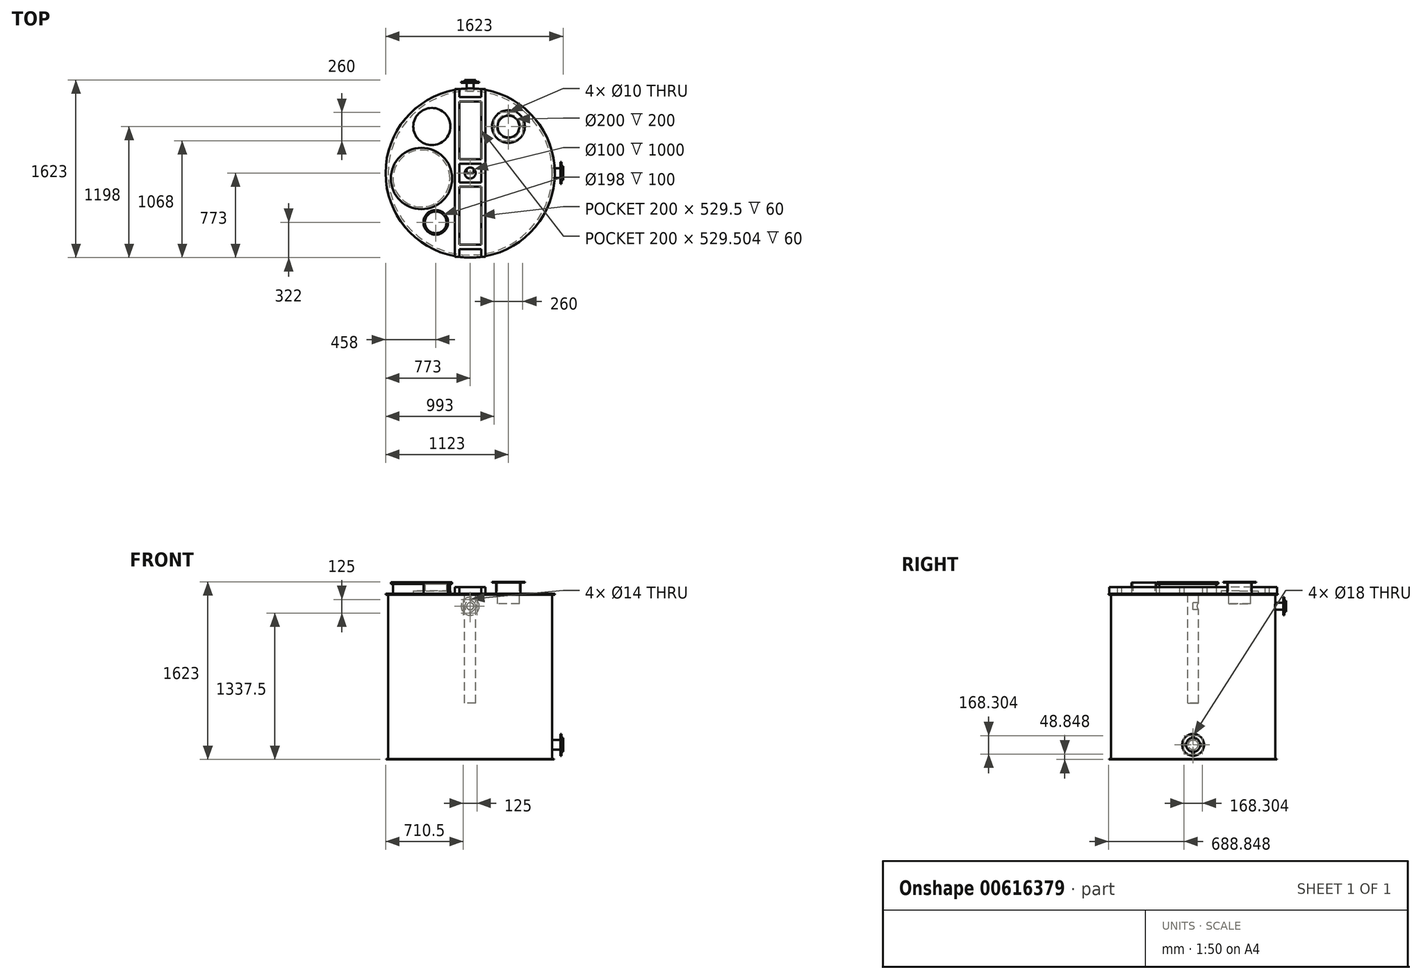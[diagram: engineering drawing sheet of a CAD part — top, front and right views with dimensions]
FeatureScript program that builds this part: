
annotation { "Feature Type Name" : "Feature", "Feature Type Description" : "" }
export const myFeature = defineFeature(function(context is Context, id is Id, definition is map)
    precondition{}
    {
        {
            var Q0;
            Q0=qCreatedBy(makeId("Front.planeOp"),FACE);
            var sketch = newSketch(context, id + "F0", { "sketchPlane" : qUnion([Q0])});
            skLineSegment(sketch, "E0.bottom", {"start": v(0, 0) * mm, "end": v(750, 0) * mm});
            skLineSegment(sketch, "E0.top", {"start": v(0, 1515) * mm, "end": v(750, 1515) * mm});
            skLineSegment(sketch, "E0.left", {"start": v(0, 0) * mm, "end": v(0, 1515) * mm});
            skLineSegment(sketch, "E0.right", {"start": v(750, 5) * mm, "end": v(750, 1505) * mm});
            skLineSegment(sketch, "E1.bottom", {"start": v(750, 0) * mm, "end": v(768.5, 0) * mm});
            skLineSegment(sketch, "E1.top", {"start": v(750, 5) * mm, "end": v(768.5, 5) * mm});
            skLineSegment(sketch, "E1.right", {"start": v(768.5, 0) * mm, "end": v(768.5, 5) * mm});
            skLineSegment(sketch, "E2.bottom", {"start": v(750, 1515) * mm, "end": v(773, 1515) * mm});
            skLineSegment(sketch, "E2.top", {"start": v(750, 1505) * mm, "end": v(773, 1505) * mm});
            skLineSegment(sketch, "E2.right", {"start": v(773, 1515) * mm, "end": v(773, 1505) * mm});
            skSolve(sketch);
        }
        {
            var Q0;
            Q0=makeQuery(id+"F0.imprint","IMPRINT",FACE,{"disambiguationData":[TD([[makeQuery(id+"F0.imprint","IMPRINT",EDGE,{"derivedFrom":sQuery(id+"F0.wireOp",EDGE,"E0.bottom")}),1.0]])]});
            var Q1;
            Q1=sQuery(id+"F0.wireOp",EDGE,"E0.left");
            revolve(context, id + "F1", {"entities" : qUnion([Q0]), "axis" : qUnion([Q1]), "revolveType" : RevolveType.FULL});
        }
        {
            var Q0;
            Q0=makeQuery(id+"F1.opRevolve","SWEPT_FACE",FACE,{"disambiguationData":[OSD([sQuery(id+"F0.wireOp",EDGE,"E0.top"),sQuery(id+"F0.wireOp",EDGE,"E2.bottom")])]});
            var sketch = newSketch(context, id + "F2", { "sketchPlane" : qUnion([Q0])});
            skLineSegment(sketch, "E3.bottom", {"start": v(-140, 766.5) * mm, "end": v(-100, 766.5) * mm});
            skLineSegment(sketch, "E3.top", {"start": v(-140, -766.5) * mm, "end": v(-100, -766.5) * mm});
            skLineSegment(sketch, "E3.left", {"start": v(-140, 766.5) * mm, "end": v(-140, -766.5) * mm});
            skLineSegment(sketch, "E3.right", {"start": v(-100, 766.5) * mm, "end": v(-100, 694.5) * mm});
            skLineSegment(sketch, "E4.bottom", {"start": v(100, 766.5) * mm, "end": v(140, 766.5) * mm});
            skLineSegment(sketch, "E4.top", {"start": v(100, -766.5) * mm, "end": v(140, -766.5) * mm});
            skLineSegment(sketch, "E4.left", {"start": v(100, 766.5) * mm, "end": v(100, 694.5) * mm});
            skLineSegment(sketch, "E4.right", {"start": v(140, 766.5) * mm, "end": v(140, -766.5) * mm});
            skLineSegment(sketch, "E5.bottom", {"start": v(-100, 694.5) * mm, "end": v(100, 694.5) * mm});
            skLineSegment(sketch, "E5.top", {"start": v(-100, 654.5) * mm, "end": v(100, 654.5) * mm});
            skLineSegment(sketch, "E6.bottom", {"start": v(-100, -654.5) * mm, "end": v(100, -654.5) * mm});
            skLineSegment(sketch, "E6.top", {"start": v(-100, -694.5) * mm, "end": v(100, -694.5) * mm});
            skLineSegment(sketch, "E7.bottom", {"start": v(-100, 125) * mm, "end": v(100, 125) * mm});
            skLineSegment(sketch, "E7.top", {"start": v(-100, 85) * mm, "end": v(100, 85) * mm});
            skLineSegment(sketch, "E8.bottom", {"start": v(-100, -85) * mm, "end": v(100, -85) * mm});
            skLineSegment(sketch, "E8.top", {"start": v(-100, -125) * mm, "end": v(100, -125) * mm});
            skLineSegment(sketch, "E9.trimOffspring", {"start": v(-100, 654.5) * mm, "end": v(-100, 125) * mm});
            skLineSegment(sketch, "E10.trimOffspring", {"start": v(100, 654.5) * mm, "end": v(100, 125) * mm});
            skLineSegment(sketch, "E11.trimOffspring", {"start": v(-100, 85) * mm, "end": v(-100, -85) * mm});
            skLineSegment(sketch, "E12.trimOffspring", {"start": v(100, 85) * mm, "end": v(100, -85) * mm});
            skLineSegment(sketch, "E13.trimOffspring", {"start": v(-100, -125) * mm, "end": v(-100, -654.5) * mm});
            skLineSegment(sketch, "E14.trimOffspring", {"start": v(100, -125) * mm, "end": v(100, -654.5) * mm});
            skLineSegment(sketch, "E15.trimOffspring", {"start": v(-100, -694.5) * mm, "end": v(-100, -766.5) * mm});
            skLineSegment(sketch, "E16.trimOffspring", {"start": v(100, -694.5) * mm, "end": v(100, -766.5) * mm});
            skSolve(sketch);
        }
        {
            var Q0;
            Q0 = qSketchRegion(id + "F2", true);
            extrude(context, id + "F3", {"entities" : qUnion([Q0]), "operationType" : NewBodyOperationType.ADD, "depth" : 60 * mm, "offsetDistance" : 25 * mm});
        }
        {
            var Q0;
            {var subQ0=sQuery(id+"F2.wireOp",EDGE,"E3.left");Q0=makeQuery(id+"F3.boolean.opBoolean","SPLIT",FACE,{"disambiguationData":[TD([makeQuery(id+"F3.opExtrude","SWEPT_FACE",FACE,{"disambiguationData":[OSD([subQ0])]})])],"derivedFrom":makeQuery(id+"F1.opRevolve","SWEPT_FACE",FACE,{"disambiguationData":[OSD([sQuery(id+"F0.wireOp",EDGE,"E0.top"),sQuery(id+"F0.wireOp",EDGE,"E2.bottom")])]})});}
            var sketch = newSketch(context, id + "F4", { "sketchPlane" : qUnion([Q0])});
            skCircle(sketch, "E17", {"center": v(-445, -50) * mm, "radius": 260 * mm});
            skSolve(sketch);
        }
        {
            var Q0;
            Q0=makeQuery(id+"F4.imprint","IMPRINT",FACE,{"disambiguationData":[TD([[makeQuery(id+"F4.imprint","IMPRINT",EDGE,{"derivedFrom":sQuery(id+"F4.wireOp",EDGE,"E17")}),1.0]])]});
            extrude(context, id + "F5", {"entities" : qUnion([Q0]), "operationType" : NewBodyOperationType.ADD, "depth" : 90 * mm, "offsetDistance" : 25 * mm});
        }
        {
            var Q0;
            {var subQ0=sQuery(id+"F2.wireOp",EDGE,"E3.left");Q0=makeQuery(id+"F3.boolean.opBoolean","SPLIT",FACE,{"disambiguationData":[TD([makeQuery(id+"F3.opExtrude","SWEPT_FACE",FACE,{"disambiguationData":[OSD([subQ0])]})])],"derivedFrom":makeQuery(id+"F1.opRevolve","SWEPT_FACE",FACE,{"disambiguationData":[OSD([sQuery(id+"F0.wireOp",EDGE,"E0.top"),sQuery(id+"F0.wireOp",EDGE,"E2.bottom")])]})});}
            var sketch = newSketch(context, id + "F6", { "sketchPlane" : qUnion([Q0])});
            skCircle(sketch, "E18", {"center": v(-350, 425) * mm, "radius": 170 * mm});
            skSolve(sketch);
        }
        {
            var Q0;
            Q0=makeQuery(id+"F6.imprint","IMPRINT",FACE,{"disambiguationData":[TD([[makeQuery(id+"F6.imprint","IMPRINT",EDGE,{"derivedFrom":sQuery(id+"F6.wireOp",EDGE,"E18")}),1.0]])]});
            extrude(context, id + "F7", {"entities" : qUnion([Q0]), "operationType" : NewBodyOperationType.ADD, "depth" : 25 * mm, "offsetDistance" : 25 * mm});
        }
        {
            var Q0;
            Q0=makeQuery(id+"F5.opExtrude","CAP_FACE",FACE,{"disambiguationData":[OSD([sQuery(id+"F4.wireOp",EDGE,"E17")])],"isStart":false});
            var sketch = newSketch(context, id + "F8", { "sketchPlane" : qUnion([Q0])});
            skCircle(sketch, "E19", {"center": v(-445, -50) * mm, "radius": 280 * mm});
            skSolve(sketch);
        }
        {
            var Q0;
            Q0 = qSketchRegion(id + "F8", true);
            extrude(context, id + "F9", {"entities" : qUnion([Q0]), "operationType" : NewBodyOperationType.ADD, "depth" : 15 * mm, "offsetDistance" : 25 * mm});
        }
        {
            var Q0;
            {var subQ0=sQuery(id+"F2.wireOp",EDGE,"E4.right");Q0=makeQuery(id+"F3.boolean.opBoolean","SPLIT",FACE,{"disambiguationData":[TD([makeQuery(id+"F3.opExtrude","SWEPT_FACE",FACE,{"disambiguationData":[OSD([subQ0])]})])],"derivedFrom":makeQuery(id+"F1.opRevolve","SWEPT_FACE",FACE,{"disambiguationData":[OSD([sQuery(id+"F0.wireOp",EDGE,"E0.top"),sQuery(id+"F0.wireOp",EDGE,"E2.bottom")])]})});}
            var sketch = newSketch(context, id + "F10", { "sketchPlane" : qUnion([Q0])});
            skCircle(sketch, "E20", {"center": v(350, 425) * mm, "radius": 111 * mm});
            skSolve(sketch);
        }
        {
            var Q0;
            Q0=makeQuery(id+"F10.imprint","IMPRINT",FACE,{"disambiguationData":[TD([[makeQuery(id+"F10.imprint","IMPRINT",EDGE,{"derivedFrom":sQuery(id+"F10.wireOp",EDGE,"E20")}),1.0]])]});
            extrude(context, id + "F11", {"entities" : qUnion([Q0]), "operationType" : NewBodyOperationType.ADD, "depth" : 100 * mm, "offsetDistance" : 25 * mm});
        }
        {
            var Q0;
            Q0=makeQuery(id+"F11.opExtrude","CAP_FACE",FACE,{"disambiguationData":[OSD([sQuery(id+"F10.wireOp",EDGE,"E20")])],"isStart":false});
            var sketch = newSketch(context, id + "F12", { "sketchPlane" : qUnion([Q0])});
            skCircle(sketch, "E21", {"center": v(350, 425) * mm, "radius": 150 * mm});
            skSolve(sketch);
        }
        {
            var Q0;
            Q0 = qSketchRegion(id + "F12", true);
            extrude(context, id + "F13", {"entities" : qUnion([Q0]), "operationType" : NewBodyOperationType.ADD, "depth" : 8 * mm, "offsetDistance" : 25 * mm});
        }
        {
            var Q0;
            Q0=makeQuery(id+"F13.opExtrude","CAP_FACE",FACE,{"disambiguationData":[OSD([sQuery(id+"F12.wireOp",EDGE,"E21")])],"isStart":false});
            var sketch = newSketch(context, id + "F14", { "sketchPlane" : qUnion([Q0])});
            skCircle(sketch, "E22", {"center": v(349.8, 555) * mm, "radius": 5 * mm});
            skCircle(sketch, "E23.1.0", {"center": v(220, 424.8) * mm, "radius": 5 * mm});
            skCircle(sketch, "E23.2.0", {"center": v(350.2, 295) * mm, "radius": 5 * mm});
            skCircle(sketch, "E23.3.0", {"center": v(480, 425.2) * mm, "radius": 5 * mm});
            skPoint(sketch, "E23.center", {"position": v(350, 425) * mm});
            skSolve(sketch);
        }
        {
            var Q0;
            Q0 = qSketchRegion(id + "F14", true);
            extrude(context, id + "F15", {"entities" : qUnion([Q0]), "operationType" : NewBodyOperationType.REMOVE, "oppositeDirection" : true, "depth" : 25 * mm, "offsetDistance" : 25 * mm});
        }
        {
            var Q0;
            Q0=makeQuery(id+"F13.opExtrude","CAP_FACE",FACE,{"disambiguationData":[OSD([sQuery(id+"F12.wireOp",EDGE,"E21")])],"isStart":false});
            var sketch = newSketch(context, id + "F16", { "sketchPlane" : qUnion([Q0])});
            skCircle(sketch, "E24", {"center": v(350, 425) * mm, "radius": 100 * mm});
            skSolve(sketch);
        }
        {
            var Q0;
            Q0=makeQuery(id+"F16.imprint","IMPRINT",FACE,{"disambiguationData":[TD([[makeQuery(id+"F16.imprint","IMPRINT",EDGE,{"derivedFrom":sQuery(id+"F16.wireOp",EDGE,"E24")}),1.0]])]});
            extrude(context, id + "F17", {"entities" : qUnion([Q0]), "operationType" : NewBodyOperationType.REMOVE, "oppositeDirection" : true, "depth" : 200 * mm, "offsetDistance" : 25 * mm});
        }
        {
            var Q0;
            Q0=makeQuery(id+"F3.boolean.opBoolean","SPLIT",FACE,{"disambiguationData":[TD([makeQuery(id+"F3.opExtrude","SWEPT_FACE",FACE,{"disambiguationData":[OSD([sQuery(id+"F2.wireOp",EDGE,"E7.top")])]})])],"derivedFrom":makeQuery(id+"F1.opRevolve","SWEPT_FACE",FACE,{"disambiguationData":[OSD([sQuery(id+"F0.wireOp",EDGE,"E0.top"),sQuery(id+"F0.wireOp",EDGE,"E2.bottom")])]})});
            var sketch = newSketch(context, id + "F18", { "sketchPlane" : qUnion([Q0])});
            skCircle(sketch, "E25", {"center": v(0, 0) * mm, "radius": 50 * mm});
            skSolve(sketch);
        }
        {
            var Q0;
            Q0=makeQuery(id+"F18.imprint","IMPRINT",FACE,{"disambiguationData":[TD([[makeQuery(id+"F18.imprint","IMPRINT",EDGE,{"derivedFrom":sQuery(id+"F18.wireOp",EDGE,"E25")}),1.0]])]});
            extrude(context, id + "F19", {"entities" : qUnion([Q0]), "operationType" : NewBodyOperationType.REMOVE, "oppositeDirection" : true, "depth" : 1000 * mm, "offsetDistance" : 25 * mm});
        }
        {
            var Q0;
            {var subQ0=sQuery(id+"F2.wireOp",EDGE,"E3.left");Q0=makeQuery(id+"F3.boolean.opBoolean","SPLIT",FACE,{"disambiguationData":[TD([makeQuery(id+"F3.opExtrude","SWEPT_FACE",FACE,{"disambiguationData":[OSD([subQ0])]})])],"derivedFrom":makeQuery(id+"F1.opRevolve","SWEPT_FACE",FACE,{"disambiguationData":[OSD([sQuery(id+"F0.wireOp",EDGE,"E0.top"),sQuery(id+"F0.wireOp",EDGE,"E2.bottom")])]})});}
            var sketch = newSketch(context, id + "F20", { "sketchPlane" : qUnion([Q0])});
            skCircle(sketch, "E26", {"center": v(-315, -451) * mm, "radius": 112.5 * mm});
            skCircle(sketch, "E27", {"center": v(-315, -451) * mm, "radius": 99 * mm});
            skSolve(sketch);
        }
        {
            var Q0;
            Q0 = qSketchRegion(id + "F20", true);
            extrude(context, id + "F21", {"entities" : qUnion([Q0]), "operationType" : NewBodyOperationType.ADD, "depth" : 100 * mm, "offsetDistance" : 25 * mm});
        }
        {
            var Q0;
            Q0=qCreatedBy(makeId("Right.planeOp"),FACE);
            var sketch = newSketch(context, id + "F22", { "sketchPlane" : qUnion([Q0])});
            skCircle(sketch, "E28", {"center": v(0, 133) * mm, "radius": 45 * mm});
            skSolve(sketch);
        }
        {
            var Q0;
            Q0 = qSketchRegion(id + "F22", true);
            extrude(context, id + "F23", {"entities" : qUnion([Q0]), "operationType" : NewBodyOperationType.ADD, "depth" : 850 * mm, "offsetDistance" : 25 * mm});
        }
        {
            var Q0;
            Q0=makeQuery(id+"F23.opExtrude","CAP_FACE",FACE,{"disambiguationData":[OSD([sQuery(id+"F22.wireOp",EDGE,"E28")])],"isStart":false});
            cPlane(context, id + "F24", {"entities" : qUnion([Q0]), "cplaneType" : CPlaneType.OFFSET, "offset" : 25 * mm, "oppositeDirection" : true, "width" : 150 * mm, "height" : 150 * mm});
        }
        {
            var Q0;
            Q0=qCreatedBy(id+"F24.planeOp",FACE);
            var sketch = newSketch(context, id + "F25", { "sketchPlane" : qUnion([Q0])});
            skCircle(sketch, "E29", {"center": v(0, 133) * mm, "radius": 100 * mm});
            skSolve(sketch);
        }
        {
            var Q0;
            Q0 = qSketchRegion(id + "F25", true);
            extrude(context, id + "F26", {"entities" : qUnion([Q0]), "operationType" : NewBodyOperationType.ADD, "depth" : 10 * mm, "offsetDistance" : 25 * mm});
        }
        {
            var Q0;
            Q0=makeQuery(id+"F26.opExtrude","CAP_FACE",FACE,{"disambiguationData":[OSD([sQuery(id+"F25.wireOp",EDGE,"E29")])],"isStart":false});
            var sketch = newSketch(context, id + "F27", { "sketchPlane" : qUnion([Q0])});
            skCircle(sketch, "E30", {"center": v(0, 133) * mm, "radius": 64.15 * mm});
            skSolve(sketch);
        }
        {
            var Q0;
            Q0=makeQuery(id+"F27.imprint","IMPRINT",FACE,{"disambiguationData":[TD([[makeQuery(id+"F27.imprint","IMPRINT",EDGE,{"derivedFrom":sQuery(id+"F27.wireOp",EDGE,"E30")}),1.0]])]});
            extrude(context, id + "F28", {"entities" : qUnion([Q0]), "operationType" : NewBodyOperationType.ADD, "depth" : 15 * mm, "offsetDistance" : 25 * mm});
        }
        {
            var Q0;
            Q0=makeQuery(id+"F26.opExtrude","CAP_FACE",FACE,{"disambiguationData":[OSD([sQuery(id+"F25.wireOp",EDGE,"E29")])],"isStart":false});
            var sketch = newSketch(context, id + "F29", { "sketchPlane" : qUnion([Q0])});
            skCircle(sketch, "E31", {"center": v(0, 217.15) * mm, "radius": 9 * mm});
            skCircle(sketch, "E32.1.0", {"center": v(-84.15, 133) * mm, "radius": 9 * mm});
            skCircle(sketch, "E32.2.0", {"center": v(0, 48.85) * mm, "radius": 9 * mm});
            skCircle(sketch, "E32.3.0", {"center": v(84.15, 133) * mm, "radius": 9 * mm});
            skPoint(sketch, "E32.center", {"position": v(0, 133) * mm});
            skSolve(sketch);
        }
        {
            var Q0;
            Q0 = qSketchRegion(id + "F29", true);
            extrude(context, id + "F30", {"entities" : qUnion([Q0]), "operationType" : NewBodyOperationType.REMOVE, "oppositeDirection" : true, "depth" : 25 * mm, "offsetDistance" : 25 * mm});
        }
        {
            var Q0;
            Q0=qCreatedBy(makeId("Front.planeOp"),FACE);
            var sketch = newSketch(context, id + "F31", { "sketchPlane" : qUnion([Q0])});
            skCircle(sketch, "E33", {"center": v(0, 1400) * mm, "radius": 32.5 * mm});
            skSolve(sketch);
        }
        {
            var Q0;
            Q0 = qSketchRegion(id + "F31", true);
            extrude(context, id + "F32", {"entities" : qUnion([Q0]), "operationType" : NewBodyOperationType.ADD, "oppositeDirection" : true, "depth" : 850 * mm, "offsetDistance" : 25 * mm});
        }
        {
            var Q0;
            Q0=makeQuery(id+"F32.opExtrude","CAP_FACE",FACE,{"disambiguationData":[OSD([sQuery(id+"F31.wireOp",EDGE,"E33")])],"isStart":false});
            cPlane(context, id + "F33", {"entities" : qUnion([Q0]), "cplaneType" : CPlaneType.OFFSET, "offset" : 25 * mm, "oppositeDirection" : true, "width" : 150 * mm, "height" : 150 * mm});
        }
        {
            var Q0;
            Q0=qCreatedBy(id+"F33.planeOp",FACE);
            var sketch = newSketch(context, id + "F34", { "sketchPlane" : qUnion([Q0])});
            skCircle(sketch, "E34", {"center": v(0, 1400) * mm, "radius": 82.5 * mm});
            skCircle(sketch, "E35", {"center": v(0, 1462.5) * mm, "radius": 7 * mm});
            skCircle(sketch, "E36.1.0", {"center": v(-62.5, 1400) * mm, "radius": 7 * mm});
            skCircle(sketch, "E36.2.0", {"center": v(0, 1337.5) * mm, "radius": 7 * mm});
            skCircle(sketch, "E36.3.0", {"center": v(62.5, 1400) * mm, "radius": 7 * mm});
            skSolve(sketch);
        }
        {
            var Q0;
            Q0=makeQuery(id+"F34.imprint","IMPRINT",FACE,{"disambiguationData":[TD([[makeQuery(id+"F34.imprint","IMPRINT",EDGE,{"derivedFrom":sQuery(id+"F34.wireOp",EDGE,"E34")}),1.0]])]});
            extrude(context, id + "F35", {"entities" : qUnion([Q0]), "operationType" : NewBodyOperationType.ADD, "depth" : 10 * mm, "offsetDistance" : 25 * mm});
        }
        {
            var Q0;
            Q0=makeQuery(id+"F32.opExtrude","CAP_FACE",FACE,{"disambiguationData":[OSD([sQuery(id+"F31.wireOp",EDGE,"E33")])],"isStart":false});
            var sketch = newSketch(context, id + "F36", { "sketchPlane" : qUnion([Q0])});
            skCircle(sketch, "E37", {"center": v(0, 1400) * mm, "radius": 50 * mm});
            skSolve(sketch);
        }
        {
            var Q0;
            Q0 = qSketchRegion(id + "F36", true);
            extrude(context, id + "F37", {"entities" : qUnion([Q0]), "operationType" : NewBodyOperationType.ADD, "oppositeDirection" : true, "depth" : 25 * mm, "offsetDistance" : 25 * mm});
        }
    });
